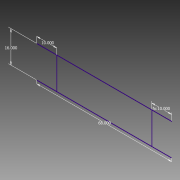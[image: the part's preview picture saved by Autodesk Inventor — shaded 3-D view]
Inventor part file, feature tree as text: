
AUTODESK INVENTOR PART (.ipt)
format: ipt  version: 2013 (Build 170138000, 138)  size: 64,000 bytes
history: native  units: in
note: dims shown in document units (in); Inventor stores cm internally (conversion verified against a paired STEP export)
features: sketch x1
ambient origin geometry x8: Origin, YZ Plane, XZ Plane, XY Plane, X Axis, Y Axis, Z Axis, Center Point
feature tree (1):
  sketch  "Sketch1"  dims[d0=68.0in d1=16.0in d2=10.0in d3=10.0in]
